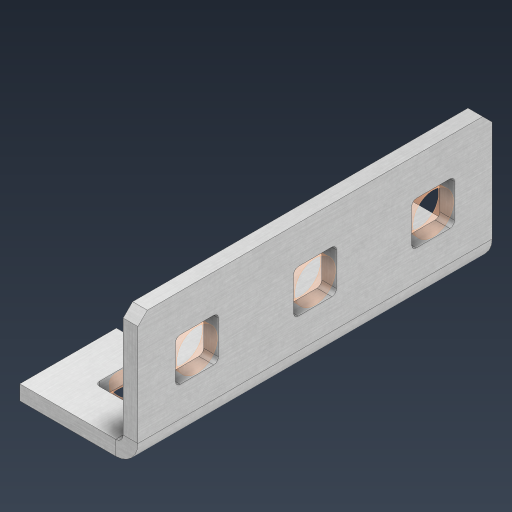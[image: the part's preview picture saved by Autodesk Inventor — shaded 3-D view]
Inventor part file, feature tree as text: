
AUTODESK INVENTOR PART (.ipt)
format: ipt  version: 2024.3 (Build 283343000, 343)  size: 453,120 bytes
history: native  units: in
note: dims shown in document units (in); Inventor stores cm internally (conversion verified against a paired STEP export)
features: other x16, sheet_metal_op x11, extrude x7, pattern_linear x2, mirror x1, chamfer x1, sketch x1
ambient origin geometry x8: Origin, YZ Plane, XZ Plane, XY Plane, X Axis, Y Axis, Z Axis, Center Point
bodies: Solid1 (feature_tree), Body (feature_tree)
feature tree (39):
  sheet_metal_op  "Flanges"
  other  "Flange Pattern Plane"
  other  "Flange Pattern Sketch"
  sheet_metal_op  "Flange Pattern"
  sheet_metal_op  "Body Pattern"
  pattern_linear  "Center Pattern"  Spacing1=1.5in  [1 undecoded]
  other  "Arc Length"
  mirror  "Notch Mirror"
  pattern_linear  "Notch Pattern"  Spacing1=0.0625in  [1 undecoded]
  chamfer  "End Chamfer"
  extrude  "Half Cut"  Depth=0.0625in
  other  "Plate1"
  sketch  "Sketch2"  dims[d0=1.0in d1=1.5in d2=0.0625in d3=0.0625in d4=0.0312in d5=0.125in d6=0.0625in d7=0.5in d8=90.0deg d9=0.0312in d10=0.25in d11=0.0625in d12=0.0625in d16=0.182in d17=0.02in d18=0.0625in d19=0.0in d20=0.25in d21=0.25in d38=1.1811in d40=0.5in d41=0.3937in d43=1.0in d46=0.172in d47=1.0in d48=0.0in d49=0.182in d50=0.02in d51=0.25in d52=0.25in d53=0.0625in d54=0.0in d55=0.172in d56=1.0in d57=0.0in d58=0.25in d60=1.1811in d62=0.5in d63=0.3937in d65=0.5in d85=0.1473in d86=0.1782in d88=0.04in d89=0.0625in d90=0.0in d91=0.04in d92=0.0491in d95=2.5in d96=0.04in d97=0.25in d98=45.0deg d99=0.25in d100=0.5in d101=0.0in d102=2.497in d106=0.182in d107=0.02in d108=0.5in d109=0.5in d110=0.0625in d111=0.0in d112=0.172in d113=0.5in d114=0.0in d117=0.5in d118=0.5in d119=0.5in]
  other  "Plate2"
  sheet_metal_op  "Bend1"
  sheet_metal_op  "Corner1"
  other  "Srf1"
  other  "Srf2"
  other  "Srf91"
  sheet_metal_op  "Body Pattern Sketch"
  other  "Srf92"
  other  "Srf786"
  other  "Srf823"
  other  "Srf856"
  other  "Srf889"
  other  "Srf890"
  sheet_metal_op  "Flange Stamp"
  sheet_metal_op  "Flange Circle"
  sheet_metal_op  "Body Stamp"
  sheet_metal_op  "Body Circle"
  other  "Center Stamp"
  other  "Center Circle"
  sheet_metal_op  "Notch"
  extrude  "ExtrusionSrf2"  Depth=0.0312in
  extrude  "ExtrusionSrf92"  Depth=0.5in
  extrude  "ExtrusionSrf823"  Depth=0.0625in
  extrude  "ExtrusionSrf856"  Depth=0.5in TaperAngle=90.0deg
  extrude  "ExtrusionSrf889"  Depth=0.25in
  extrude  "ExtrusionSrf890"  Depth=0.0625in
note: 2 required parameter values undecoded (feature->parameter linkage not recoverable at this tier; creation-order binding heuristic only, values carry confidence <= 0.55)
